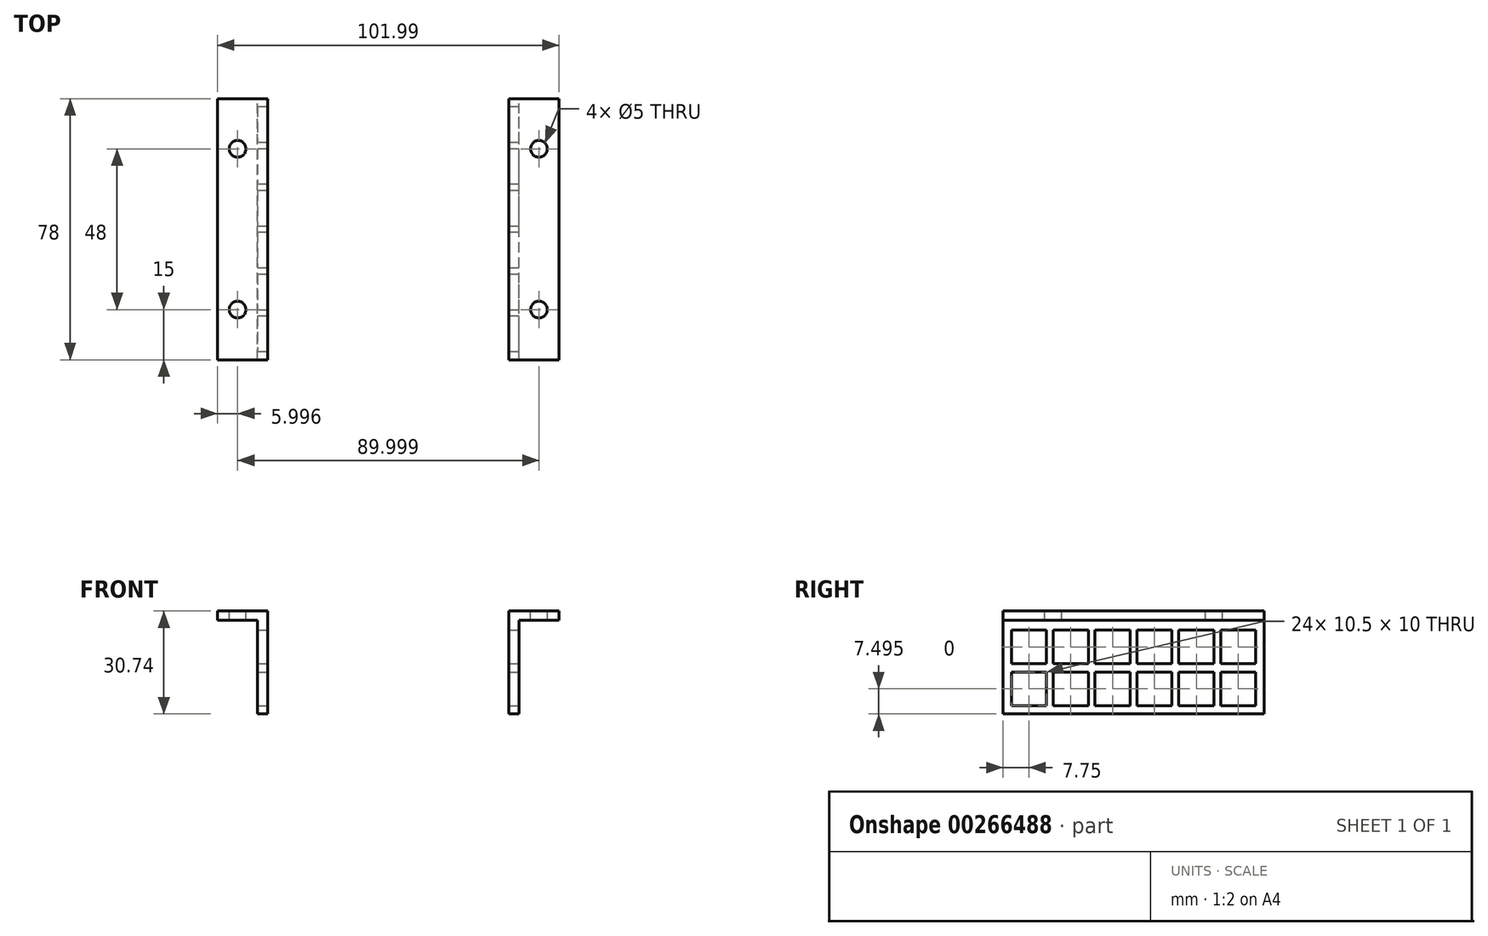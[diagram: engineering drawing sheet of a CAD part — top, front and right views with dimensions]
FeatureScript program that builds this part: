
annotation { "Feature Type Name" : "Feature", "Feature Type Description" : "" }
export const myFeature = defineFeature(function(context is Context, id is Id, definition is map)
    precondition{}
    {
        {
            var Q0;
            Q0=qCreatedBy(makeId("Front.planeOp"),FACE);
            var sketch = newSketch(context, id + "F0", { "sketchPlane" : qUnion([Q0])});
            skLineSegment(sketch, "E0", {"start": v(36.03, -9.62) * mm, "end": v(36.03, 18.38) * mm});
            skLineSegment(sketch, "E1", {"start": v(36.03, 18.38) * mm, "end": v(48.02, 18.38) * mm});
            skLineSegment(sketch, "E2", {"start": v(48.02, 18.38) * mm, "end": v(48.02, 21.12) * mm});
            skLineSegment(sketch, "E3", {"start": v(48.02, 21.12) * mm, "end": v(33.02, 21.12) * mm});
            skLineSegment(sketch, "E4", {"start": v(33.02, 21.12) * mm, "end": v(33.02, -9.62) * mm});
            skLineSegment(sketch, "E5.MirrorCS", {"start": v(-53.97, 18.38) * mm, "end": v(-53.97, 21.12) * mm});
            skLineSegment(sketch, "E6.MirrorCS", {"start": v(-41.97, -9.62) * mm, "end": v(-41.97, 18.38) * mm});
            skLineSegment(sketch, "E7.MirrorCS", {"start": v(-41.97, 18.38) * mm, "end": v(-53.97, 18.38) * mm});
            skLineSegment(sketch, "E8.MirrorCS", {"start": v(-53.97, 21.12) * mm, "end": v(-38.97, 21.12) * mm});
            skLineSegment(sketch, "E9.MirrorCS", {"start": v(-38.97, 21.12) * mm, "end": v(-38.97, -9.62) * mm});
            skPoint(sketch, "E10.MirrorCS.start.orphan", {"position": v(36.03, 18.38) * mm});
            skLineSegment(sketch, "E11", {"start": v(-41.97, -9.62) * mm, "end": v(-38.97, -9.62) * mm});
            skLineSegment(sketch, "E12", {"start": v(36.03, -9.62) * mm, "end": v(33.02, -9.62) * mm});
            skSolve(sketch);
        }
        {
            var Q0;
            Q0=qSketchRegion(id+"F0",true);
            extrude(context, id + "F1", {"entities" : qUnion([Q0]), "endBound" : BoundingType.SYMMETRIC, "depth" : 78 * mm});
        }
        {
            var Q0;
            Q0=makeQuery(id+"F1.opExtrude","SWEPT_FACE",FACE,{"disambiguationData":[OSD([sQuery(id+"F0.wireOp",EDGE,"E3")])]});
            var sketch = newSketch(context, id + "F2", { "sketchPlane" : qUnion([Q0])});
            skLineSegment(sketch, "E13", {"start": v(42.02, -39) * mm, "end": v(42.02, 39) * mm, "construction": true});
            skLineSegment(sketch, "E14.0.0", {"start": v(-38.97, 39) * mm, "end": v(-53.97, 39) * mm, "construction": true});
            skLineSegment(sketch, "E14.0.1", {"start": v(-53.97, 39) * mm, "end": v(-53.97, -39) * mm, "construction": true});
            skLineSegment(sketch, "E14.0.2", {"start": v(-53.97, -39) * mm, "end": v(-38.97, -39) * mm, "construction": true});
            skLineSegment(sketch, "E14.0.3", {"start": v(-38.97, -39) * mm, "end": v(-38.97, 39) * mm, "construction": true});
            skLineSegment(sketch, "E15", {"start": v(-47.97, 39) * mm, "end": v(-47.97, -39) * mm, "construction": true});
            skLineSegment(sketch, "E16", {"start": v(-53.97, -24) * mm, "end": v(48.02, -24) * mm, "construction": true});
            skLineSegment(sketch, "E17", {"start": v(48.02, 24) * mm, "end": v(-53.97, 24) * mm, "construction": true});
            skLineSegment(sketch, "E18", {"start": v(48.02, -24) * mm, "end": v(48.02, -39) * mm, "construction": true});
            skLineSegment(sketch, "E19", {"start": v(48.02, 39) * mm, "end": v(48.02, 24) * mm, "construction": true});
            skCircle(sketch, "E20", {"center": v(42.02, -24) * mm, "radius": 2.5 * mm});
            skCircle(sketch, "E21", {"center": v(42.02, 24) * mm, "radius": 2.5 * mm});
            skCircle(sketch, "E22", {"center": v(-47.97, 24) * mm, "radius": 2.5 * mm});
            skCircle(sketch, "E23", {"center": v(-47.97, -24) * mm, "radius": 2.5 * mm});
            skSolve(sketch);
        }
        {
            var Q0;
            Q0=qSketchRegion(id+"F2",true);
            extrude(context, id + "F3", {"entities" : qUnion([Q0]), "operationType" : NewBodyOperationType.REMOVE, "endBound" : BoundingType.UP_TO_NEXT, "oppositeDirection" : true, "depth" : 25 * mm});
        }
        {
            var Q0;
            Q0=makeQuery(id+"F1.opExtrude","SWEPT_FACE",FACE,{"disambiguationData":[OSD([sQuery(id+"F0.wireOp",EDGE,"E0")])]});
            var sketch = newSketch(context, id + "F4", { "sketchPlane" : qUnion([Q0])});
            skLineSegment(sketch, "E24.bottom", {"start": v(-36.5, -7.12) * mm, "end": v(-26.5, -7.12) * mm});
            skLineSegment(sketch, "E24.top", {"start": v(-36.5, 2.88) * mm, "end": v(-26.5, 2.88) * mm});
            skLineSegment(sketch, "E24.left", {"start": v(-36.5, -7.12) * mm, "end": v(-36.5, 2.88) * mm});
            skLineSegment(sketch, "E24.right", {"start": v(-26.5, -7.12) * mm, "end": v(-26.5, 2.88) * mm});
            skLineSegment(sketch, "E25.0.1.0", {"start": v(-36.5, 5.38) * mm, "end": v(-36.5, 15.38) * mm});
            skLineSegment(sketch, "E25.0.1.1", {"start": v(-26.5, 5.38) * mm, "end": v(-26.5, 15.38) * mm});
            skLineSegment(sketch, "E25.0.1.2", {"start": v(-36.5, 5.38) * mm, "end": v(-26.5, 5.38) * mm});
            skLineSegment(sketch, "E25.0.1.3", {"start": v(-36.5, 15.38) * mm, "end": v(-26.5, 15.38) * mm});
            skLineSegment(sketch, "E25.1.0.0", {"start": v(-24, -7.12) * mm, "end": v(-24, 2.88) * mm});
            skLineSegment(sketch, "E25.1.0.1", {"start": v(-14, -7.12) * mm, "end": v(-14, 2.88) * mm});
            skLineSegment(sketch, "E25.1.0.2", {"start": v(-24, -7.12) * mm, "end": v(-14, -7.12) * mm});
            skLineSegment(sketch, "E25.1.0.3", {"start": v(-24, 2.88) * mm, "end": v(-14, 2.88) * mm});
            skLineSegment(sketch, "E25.1.1.0", {"start": v(-24, 5.38) * mm, "end": v(-24, 15.38) * mm});
            skLineSegment(sketch, "E25.1.1.1", {"start": v(-14, 5.38) * mm, "end": v(-14, 15.38) * mm});
            skLineSegment(sketch, "E25.1.1.2", {"start": v(-24, 5.38) * mm, "end": v(-14, 5.38) * mm});
            skLineSegment(sketch, "E25.1.1.3", {"start": v(-24, 15.38) * mm, "end": v(-14, 15.38) * mm});
            skLineSegment(sketch, "E25.2.0.0", {"start": v(-11.5, -7.12) * mm, "end": v(-11.5, 2.88) * mm});
            skLineSegment(sketch, "E25.2.0.1", {"start": v(-1.5, -7.12) * mm, "end": v(-1.5, 2.88) * mm});
            skLineSegment(sketch, "E25.2.0.2", {"start": v(-11.5, -7.12) * mm, "end": v(-1.5, -7.12) * mm});
            skLineSegment(sketch, "E25.2.0.3", {"start": v(-11.5, 2.88) * mm, "end": v(-1.5, 2.88) * mm});
            skLineSegment(sketch, "E25.2.1.0", {"start": v(-11.5, 5.38) * mm, "end": v(-11.5, 15.38) * mm});
            skLineSegment(sketch, "E25.2.1.1", {"start": v(-1.5, 5.38) * mm, "end": v(-1.5, 15.38) * mm});
            skLineSegment(sketch, "E25.2.1.2", {"start": v(-11.5, 5.38) * mm, "end": v(-1.5, 5.38) * mm});
            skLineSegment(sketch, "E25.2.1.3", {"start": v(-11.5, 15.38) * mm, "end": v(-1.5, 15.38) * mm});
            skLineSegment(sketch, "E25.3.0.0", {"start": v(1, -7.12) * mm, "end": v(1, 2.88) * mm});
            skLineSegment(sketch, "E25.3.0.1", {"start": v(11, -7.12) * mm, "end": v(11, 2.88) * mm});
            skLineSegment(sketch, "E25.3.0.2", {"start": v(1, -7.12) * mm, "end": v(11, -7.12) * mm});
            skLineSegment(sketch, "E25.3.0.3", {"start": v(1, 2.88) * mm, "end": v(11, 2.88) * mm});
            skLineSegment(sketch, "E25.3.1.0", {"start": v(1, 5.38) * mm, "end": v(1, 15.38) * mm});
            skLineSegment(sketch, "E25.3.1.1", {"start": v(11, 5.38) * mm, "end": v(11, 15.38) * mm});
            skLineSegment(sketch, "E25.3.1.2", {"start": v(1, 5.38) * mm, "end": v(11, 5.38) * mm});
            skLineSegment(sketch, "E25.3.1.3", {"start": v(1, 15.38) * mm, "end": v(11, 15.38) * mm});
            skLineSegment(sketch, "E25.4.0.0", {"start": v(13.5, -7.12) * mm, "end": v(13.5, 2.88) * mm});
            skLineSegment(sketch, "E25.4.0.1", {"start": v(23.5, -7.12) * mm, "end": v(23.5, 2.88) * mm});
            skLineSegment(sketch, "E25.4.0.2", {"start": v(13.5, -7.12) * mm, "end": v(23.5, -7.12) * mm});
            skLineSegment(sketch, "E25.4.0.3", {"start": v(13.5, 2.88) * mm, "end": v(23.5, 2.88) * mm});
            skLineSegment(sketch, "E25.4.1.0", {"start": v(13.5, 5.38) * mm, "end": v(13.5, 15.38) * mm});
            skLineSegment(sketch, "E25.4.1.1", {"start": v(23.5, 5.38) * mm, "end": v(23.5, 15.38) * mm});
            skLineSegment(sketch, "E25.4.1.2", {"start": v(13.5, 5.38) * mm, "end": v(23.5, 5.38) * mm});
            skLineSegment(sketch, "E25.4.1.3", {"start": v(13.5, 15.38) * mm, "end": v(23.5, 15.38) * mm});
            skLineSegment(sketch, "E25.5.0.0", {"start": v(26, -7.12) * mm, "end": v(26, 2.88) * mm});
            skLineSegment(sketch, "E25.5.0.1", {"start": v(36, -7.12) * mm, "end": v(36, 2.88) * mm});
            skLineSegment(sketch, "E25.5.0.2", {"start": v(26, -7.12) * mm, "end": v(36, -7.12) * mm});
            skLineSegment(sketch, "E25.5.0.3", {"start": v(26, 2.88) * mm, "end": v(36, 2.88) * mm});
            skLineSegment(sketch, "E25.5.1.0", {"start": v(26, 5.38) * mm, "end": v(26, 15.38) * mm});
            skLineSegment(sketch, "E25.5.1.1", {"start": v(36, 5.38) * mm, "end": v(36, 15.38) * mm});
            skLineSegment(sketch, "E25.5.1.2", {"start": v(26, 5.38) * mm, "end": v(36, 5.38) * mm});
            skLineSegment(sketch, "E25.5.1.3", {"start": v(26, 15.38) * mm, "end": v(36, 15.38) * mm});
            skLineSegment(sketch, "E25.direction1", {"start": v(-36.5, -7.12) * mm, "end": v(-24, -7.12) * mm, "construction": true});
            skLineSegment(sketch, "E25.direction2", {"start": v(-36.5, -7.12) * mm, "end": v(-36.5, 5.38) * mm, "construction": true});
            skSolve(sketch);
        }
        {
            var Q0;
            Q0 = qSketchRegion(id + "F4", true);
            var Q1;
            Q1=makeQuery(id+"F1.opExtrude","SWEPT_FACE",FACE,{"disambiguationData":[OSD([sQuery(id+"F0.wireOp",EDGE,"E6.MirrorCS")])]});
            extrude(context, id + "F5", {"entities" : qUnion([Q0]), "operationType" : NewBodyOperationType.REMOVE, "endBound" : BoundingType.THROUGH_ALL, "oppositeDirection" : true, "endBoundEntityFace" : qUnion([Q1]), "depth" : 86.9 * mm});
        }
        {
            var Q0;
            Q0=makeQuery(id+"F1.opExtrude","SWEPT_FACE",FACE,{"disambiguationData":[OSD([sQuery(id+"F0.wireOp",EDGE,"E6.MirrorCS")])]});
            var sketch = newSketch(context, id + "F6", { "sketchPlane" : qUnion([Q0])});
            skLineSegment(sketch, "E26.bottom", {"start": v(-36.5, -7.12) * mm, "end": v(-26.5, -7.12) * mm});
            skLineSegment(sketch, "E26.top", {"start": v(-36.5, 2.88) * mm, "end": v(-26.5, 2.88) * mm});
            skLineSegment(sketch, "E26.left", {"start": v(-36.5, -7.12) * mm, "end": v(-36.5, 2.88) * mm});
            skLineSegment(sketch, "E26.right", {"start": v(-26.5, -7.12) * mm, "end": v(-26.5, 2.88) * mm});
            skLineSegment(sketch, "E27.0.1.0", {"start": v(-36.5, 5.38) * mm, "end": v(-26.5, 5.38) * mm});
            skLineSegment(sketch, "E27.0.1.1", {"start": v(-36.5, 15.38) * mm, "end": v(-26.5, 15.38) * mm});
            skLineSegment(sketch, "E27.0.1.2", {"start": v(-36.5, 5.38) * mm, "end": v(-36.5, 15.38) * mm});
            skLineSegment(sketch, "E27.0.1.3", {"start": v(-26.5, 5.38) * mm, "end": v(-26.5, 15.38) * mm});
            skLineSegment(sketch, "E27.1.0.0", {"start": v(-24, -7.12) * mm, "end": v(-14, -7.12) * mm});
            skLineSegment(sketch, "E27.1.0.1", {"start": v(-24, 2.88) * mm, "end": v(-14, 2.88) * mm});
            skLineSegment(sketch, "E27.1.0.2", {"start": v(-24, -7.12) * mm, "end": v(-24, 2.88) * mm});
            skLineSegment(sketch, "E27.1.0.3", {"start": v(-14, -7.12) * mm, "end": v(-14, 2.88) * mm});
            skLineSegment(sketch, "E27.1.1.0", {"start": v(-24, 5.38) * mm, "end": v(-14, 5.38) * mm});
            skLineSegment(sketch, "E27.1.1.1", {"start": v(-24, 15.38) * mm, "end": v(-14, 15.38) * mm});
            skLineSegment(sketch, "E27.1.1.2", {"start": v(-24, 5.38) * mm, "end": v(-24, 15.38) * mm});
            skLineSegment(sketch, "E27.1.1.3", {"start": v(-14, 5.38) * mm, "end": v(-14, 15.38) * mm});
            skLineSegment(sketch, "E27.2.0.0", {"start": v(-11.5, -7.12) * mm, "end": v(-1.5, -7.12) * mm});
            skLineSegment(sketch, "E27.2.0.1", {"start": v(-11.5, 2.88) * mm, "end": v(-1.5, 2.88) * mm});
            skLineSegment(sketch, "E27.2.0.2", {"start": v(-11.5, -7.12) * mm, "end": v(-11.5, 2.88) * mm});
            skLineSegment(sketch, "E27.2.0.3", {"start": v(-1.5, -7.12) * mm, "end": v(-1.5, 2.88) * mm});
            skLineSegment(sketch, "E27.2.1.0", {"start": v(-11.5, 5.38) * mm, "end": v(-1.5, 5.38) * mm});
            skLineSegment(sketch, "E27.2.1.1", {"start": v(-11.5, 15.38) * mm, "end": v(-1.5, 15.38) * mm});
            skLineSegment(sketch, "E27.2.1.2", {"start": v(-11.5, 5.38) * mm, "end": v(-11.5, 15.38) * mm});
            skLineSegment(sketch, "E27.2.1.3", {"start": v(-1.5, 5.38) * mm, "end": v(-1.5, 15.38) * mm});
            skLineSegment(sketch, "E27.3.0.0", {"start": v(1, -7.12) * mm, "end": v(11, -7.12) * mm});
            skLineSegment(sketch, "E27.3.0.1", {"start": v(1, 2.88) * mm, "end": v(11, 2.88) * mm});
            skLineSegment(sketch, "E27.3.0.2", {"start": v(1, -7.12) * mm, "end": v(1, 2.88) * mm});
            skLineSegment(sketch, "E27.3.0.3", {"start": v(11, -7.12) * mm, "end": v(11, 2.88) * mm});
            skLineSegment(sketch, "E27.3.1.0", {"start": v(1, 5.38) * mm, "end": v(11, 5.38) * mm});
            skLineSegment(sketch, "E27.3.1.1", {"start": v(1, 15.38) * mm, "end": v(11, 15.38) * mm});
            skLineSegment(sketch, "E27.3.1.2", {"start": v(1, 5.38) * mm, "end": v(1, 15.38) * mm});
            skLineSegment(sketch, "E27.3.1.3", {"start": v(11, 5.38) * mm, "end": v(11, 15.38) * mm});
            skLineSegment(sketch, "E27.4.0.0", {"start": v(13.5, -7.12) * mm, "end": v(23.5, -7.12) * mm});
            skLineSegment(sketch, "E27.4.0.1", {"start": v(13.5, 2.88) * mm, "end": v(23.5, 2.88) * mm});
            skLineSegment(sketch, "E27.4.0.2", {"start": v(13.5, -7.12) * mm, "end": v(13.5, 2.88) * mm});
            skLineSegment(sketch, "E27.4.0.3", {"start": v(23.5, -7.12) * mm, "end": v(23.5, 2.88) * mm});
            skLineSegment(sketch, "E27.4.1.0", {"start": v(13.5, 5.38) * mm, "end": v(23.5, 5.38) * mm});
            skLineSegment(sketch, "E27.4.1.1", {"start": v(13.5, 15.38) * mm, "end": v(23.5, 15.38) * mm});
            skLineSegment(sketch, "E27.4.1.2", {"start": v(13.5, 5.38) * mm, "end": v(13.5, 15.38) * mm});
            skLineSegment(sketch, "E27.4.1.3", {"start": v(23.5, 5.38) * mm, "end": v(23.5, 15.38) * mm});
            skLineSegment(sketch, "E27.5.0.0", {"start": v(26, -7.12) * mm, "end": v(36, -7.12) * mm});
            skLineSegment(sketch, "E27.5.0.1", {"start": v(26, 2.88) * mm, "end": v(36, 2.88) * mm});
            skLineSegment(sketch, "E27.5.0.2", {"start": v(26, -7.12) * mm, "end": v(26, 2.88) * mm});
            skLineSegment(sketch, "E27.5.0.3", {"start": v(36, -7.12) * mm, "end": v(36, 2.88) * mm});
            skLineSegment(sketch, "E27.5.1.0", {"start": v(26, 5.38) * mm, "end": v(36, 5.38) * mm});
            skLineSegment(sketch, "E27.5.1.1", {"start": v(26, 15.38) * mm, "end": v(36, 15.38) * mm});
            skLineSegment(sketch, "E27.5.1.2", {"start": v(26, 5.38) * mm, "end": v(26, 15.38) * mm});
            skLineSegment(sketch, "E27.5.1.3", {"start": v(36, 5.38) * mm, "end": v(36, 15.38) * mm});
            skLineSegment(sketch, "E27.direction1", {"start": v(-36.5, -7.12) * mm, "end": v(-24, -7.12) * mm, "construction": true});
            skLineSegment(sketch, "E27.direction2", {"start": v(-36.5, -7.12) * mm, "end": v(-36.5, 5.38) * mm, "construction": true});
            skSolve(sketch);
        }
        {
            var Q0;
            Q0 = qSketchRegion(id + "F6", true);
            extrude(context, id + "F7", {"entities" : qUnion([Q0]), "operationType" : NewBodyOperationType.REMOVE, "endBound" : BoundingType.THROUGH_ALL, "oppositeDirection" : true, "depth" : 25 * mm});
        }
    });
